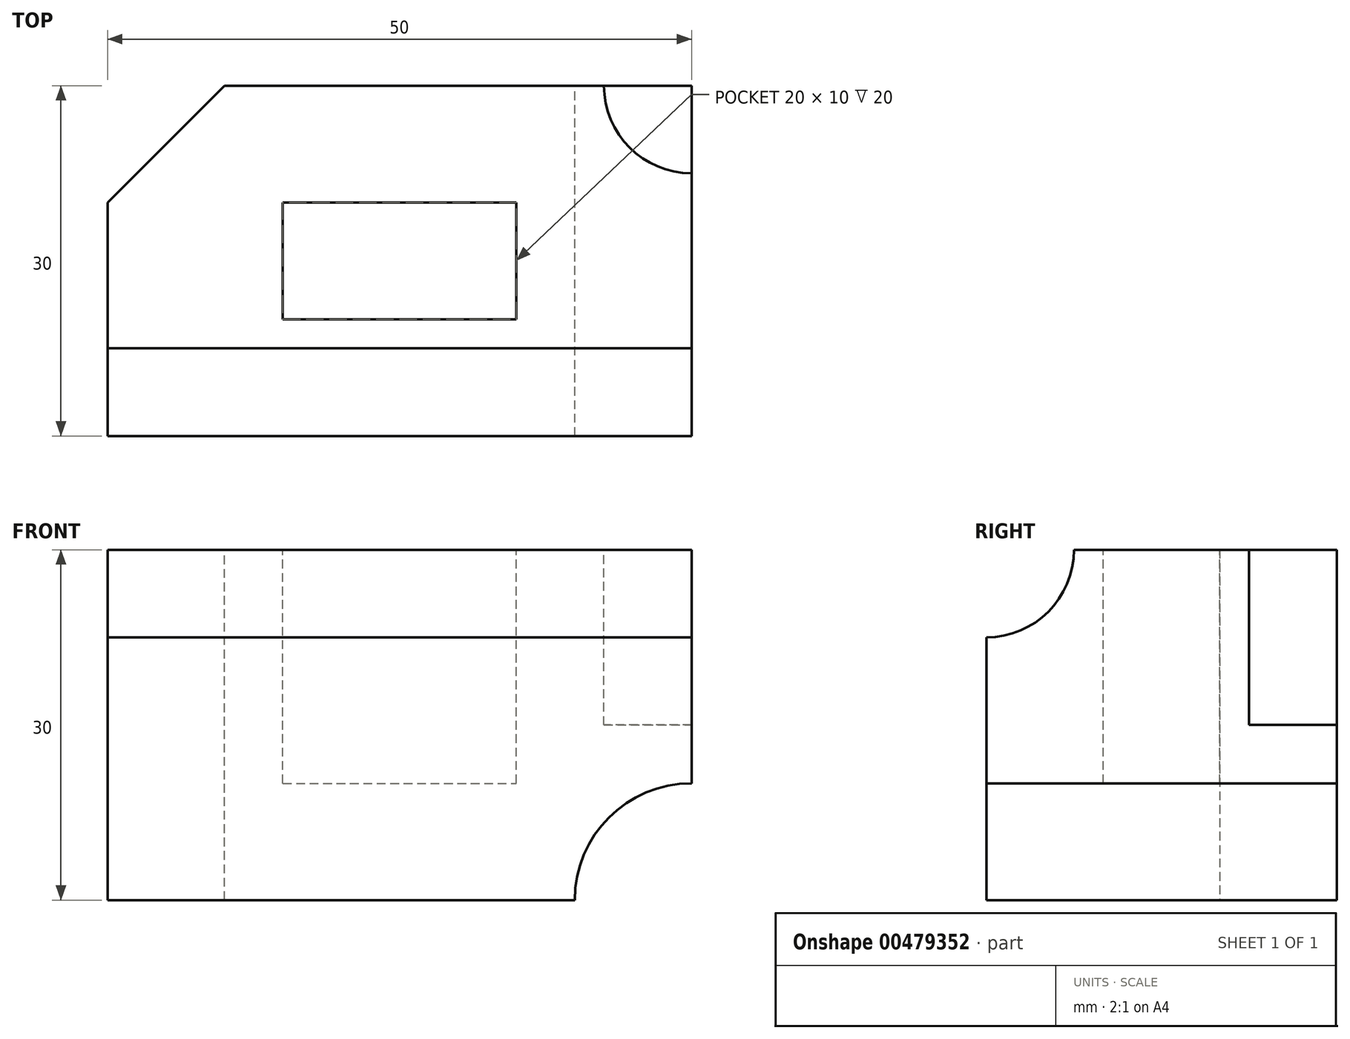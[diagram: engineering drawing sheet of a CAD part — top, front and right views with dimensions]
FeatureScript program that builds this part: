
annotation { "Feature Type Name" : "Feature", "Feature Type Description" : "" }
export const myFeature = defineFeature(function(context is Context, id is Id, definition is map)
    precondition{}
    {
        {
            var Q0;
            Q0=qCreatedBy(makeId("Front.planeOp"),FACE);
            var sketch = newSketch(context, id + "F0", { "sketchPlane" : qUnion([Q0])});
            skLineSegment(sketch, "E0.bottom", {"start": v(0, 0) * mm, "end": v(50, 0) * mm});
            skLineSegment(sketch, "E0.top", {"start": v(0, 30) * mm, "end": v(50, 30) * mm});
            skLineSegment(sketch, "E0.left", {"start": v(0, 0) * mm, "end": v(0, 30) * mm});
            skLineSegment(sketch, "E0.right", {"start": v(50, 0) * mm, "end": v(50, 30) * mm});
            skSolve(sketch);
        }
        {
            var Q0;
            Q0 = qSketchRegion(id + "F0", true);
            extrude(context, id + "F1", {"entities" : qUnion([Q0]), "oppositeDirection" : true, "depth" : 30 * mm});
        }
        {
            var Q0;
            Q0=makeQuery(id+"F1.opExtrude","SWEPT_FACE",FACE,{"disambiguationData":[OSD([sQuery(id+"F0.wireOp",EDGE,"E0.top")])]});
            var sketch = newSketch(context, id + "F2", { "sketchPlane" : qUnion([Q0])});
            skLineSegment(sketch, "E1.bottom", {"start": v(15, 20) * mm, "end": v(35, 20) * mm});
            skLineSegment(sketch, "E1.top", {"start": v(15, 10) * mm, "end": v(35, 10) * mm});
            skLineSegment(sketch, "E1.left", {"start": v(15, 20) * mm, "end": v(15, 10) * mm});
            skLineSegment(sketch, "E1.right", {"start": v(35, 20) * mm, "end": v(35, 10) * mm});
            skSolve(sketch);
        }
        {
            var Q0;
            Q0 = qSketchRegion(id + "F2", true);
            extrude(context, id + "F3", {"entities" : qUnion([Q0]), "operationType" : NewBodyOperationType.REMOVE, "oppositeDirection" : true, "depth" : 20 * mm});
        }
        {
            var Q0;
            Q0=makeQuery(id+"F1.opExtrude","CAP_EDGE",EDGE,{"disambiguationData":[OSD([sQuery(id+"F0.wireOp",EDGE,"E0.left")])],"isStart":false});
            chamfer(context, id + "F4", {"entities" : qUnion([Q0]), "width" : 10 * mm, "tangentPropagation" : true});
        }
        {
            var Q0;
            Q0=makeQuery(id+"F1.opExtrude","SWEPT_FACE",FACE,{"disambiguationData":[OSD([sQuery(id+"F0.wireOp",EDGE,"E0.top")])]});
            var sketch = newSketch(context, id + "F5", { "sketchPlane" : qUnion([Q0])});
            skCircle(sketch, "E2", {"center": v(50, 30) * mm, "radius": 7.5 * mm});
            skSolve(sketch);
        }
        {
            var Q0;
            Q0 = qSketchRegion(id + "F5", true);
            extrude(context, id + "F6", {"entities" : qUnion([Q0]), "operationType" : NewBodyOperationType.REMOVE, "oppositeDirection" : true, "depth" : 15 * mm});
        }
        {
            var Q0;
            Q0=makeQuery(id+"F1.opExtrude","SWEPT_FACE",FACE,{"disambiguationData":[OSD([sQuery(id+"F0.wireOp",EDGE,"E0.right")])]});
            var sketch = newSketch(context, id + "F7", { "sketchPlane" : qUnion([Q0])});
            skCircle(sketch, "E3", {"center": v(0, 30) * mm, "radius": 7.5 * mm});
            skSolve(sketch);
        }
        {
            var Q0;
            Q0 = qSketchRegion(id + "F7", true);
            var Q1;
            Q1=makeQuery(id+"F1.opExtrude","SWEPT_FACE",FACE,{"disambiguationData":[OSD([sQuery(id+"F0.wireOp",EDGE,"E0.left")])]});
            extrude(context, id + "F8", {"entities" : qUnion([Q0]), "operationType" : NewBodyOperationType.REMOVE, "endBound" : BoundingType.UP_TO_SURFACE, "oppositeDirection" : true, "endBoundEntityFace" : qUnion([Q1]), "depth" : 25 * mm});
        }
        {
            var Q0;
            Q0=makeQuery(id+"F1.opExtrude","CAP_FACE",FACE,{"disambiguationData":[OSD([sQuery(id+"F0.wireOp",EDGE,"E0.bottom"),sQuery(id+"F0.wireOp",EDGE,"E0.top"),sQuery(id+"F0.wireOp",EDGE,"E0.left"),sQuery(id+"F0.wireOp",EDGE,"E0.right")])],"isStart":false});
            var sketch = newSketch(context, id + "F9", { "sketchPlane" : qUnion([Q0])});
            skCircle(sketch, "E4", {"center": v(-50, 0) * mm, "radius": 10 * mm});
            skSolve(sketch);
        }
        {
            var Q0;
            Q0 = qSketchRegion(id + "F9", true);
            var Q1;
            Q1=makeQuery(id+"F1.opExtrude","CAP_FACE",FACE,{"disambiguationData":[OSD([sQuery(id+"F0.wireOp",EDGE,"E0.bottom"),sQuery(id+"F0.wireOp",EDGE,"E0.top"),sQuery(id+"F0.wireOp",EDGE,"E0.left"),sQuery(id+"F0.wireOp",EDGE,"E0.right")])],"isStart":true});
            extrude(context, id + "F10", {"entities" : qUnion([Q0]), "operationType" : NewBodyOperationType.REMOVE, "endBound" : BoundingType.UP_TO_SURFACE, "oppositeDirection" : true, "endBoundEntityFace" : qUnion([Q1]), "depth" : 25 * mm});
        }
    });
